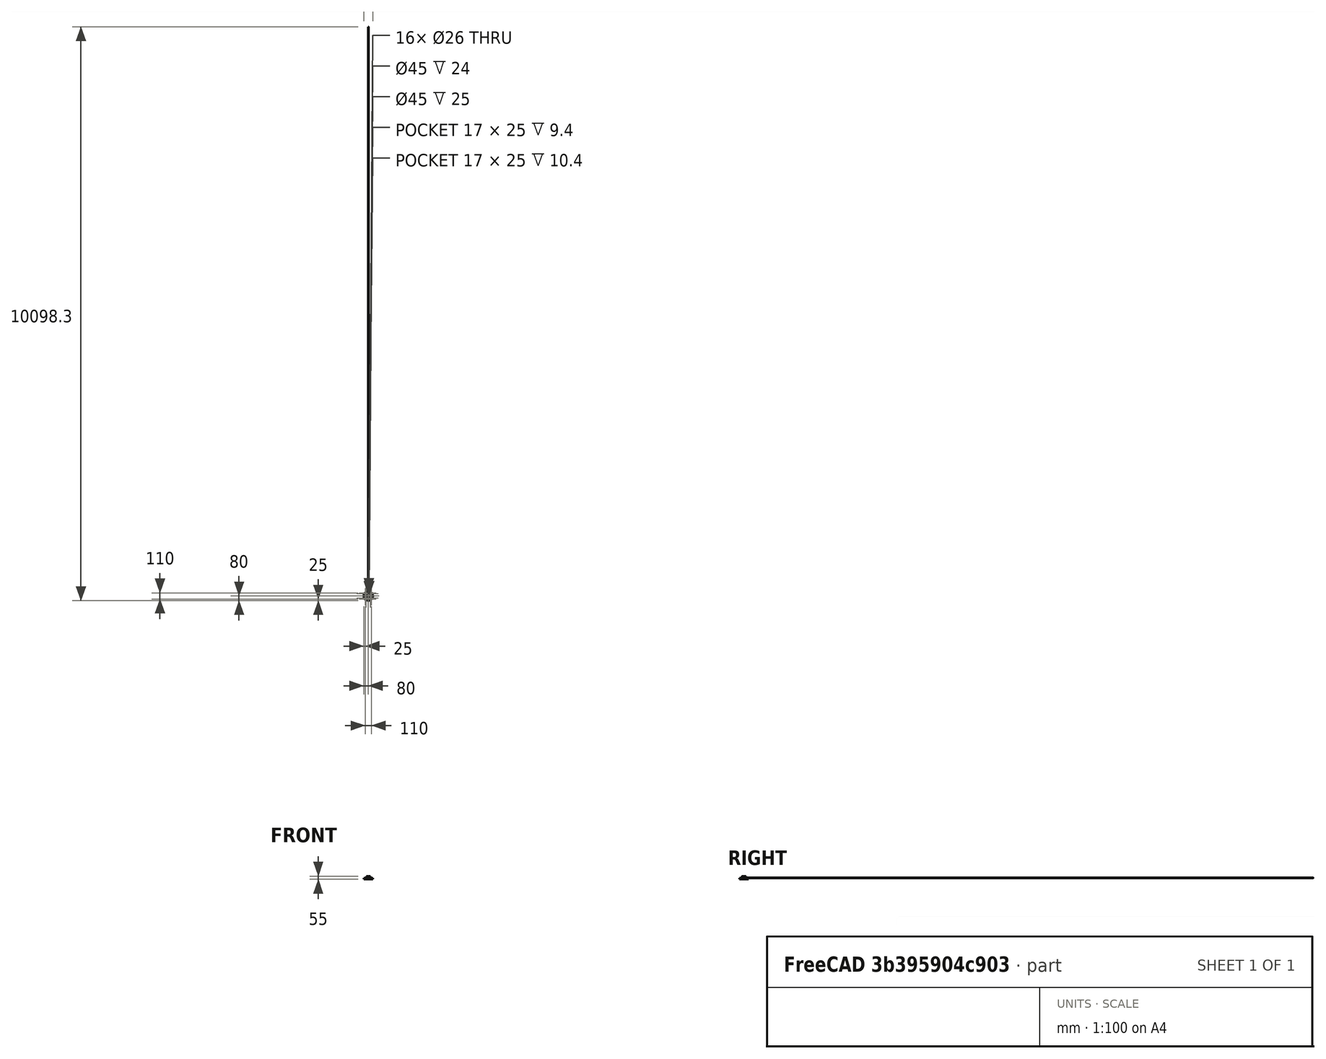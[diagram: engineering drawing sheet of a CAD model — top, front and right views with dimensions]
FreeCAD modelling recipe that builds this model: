
FCSTD DOCUMENT  (FreeCAD 0.16R)
Label: tubknobtest
License: All rights reserved
LicenseURL: http://en.wikipedia.org/wiki/All_rights_reserved
objects: Sketcher::SketchObject×9, PartDesign::Pocket×6, PartDesign::Pad×2, PartDesign::Chamfer×2, PartDesign::PolarPattern×1, PartDesign::Fillet×1, Mesh::Feature×1
note: 29 computed .brp shape members not serialized (recipe doc carries the construction recipe); baked Part::Feature solids carry a one-line shape summary decoded from their .brp

FEATURE [Sketcher::SketchObject] Sketch
  sketch-geometry (1):
    g0: Circle CenterX=0 CenterY=0 CenterZ=0 NormalX=0 NormalY=0 NormalZ=1 Radius=80
  constraints (2):
    c: Coincident(g0,g-1)
    c: Radius(g0) = 80
FEATURE [PartDesign::Pad] Pad
  Length = 20
  Length2 = 100
  Sketch = -> Sketch
  Type = 0
FEATURE [Sketcher::SketchObject] Sketch001
  Placement = pos=(0,0,20) rot=(0,0,1;0rad)
  Support = -> Pad [Face3]
  sketch-geometry (1):
    g0: Circle CenterX=0 CenterY=0 CenterZ=0 NormalX=0 NormalY=0 NormalZ=1 Radius=34
  constraints (2):
    c: Coincident(g0,g-1)
    c: Radius(g0) = 34
FEATURE [PartDesign::Pad] Pad001
  Length = 35
  Length2 = 100
  Sketch = -> Sketch001
  Type = 0
FEATURE [Sketcher::SketchObject] Sketch002
  Placement = pos=(0,0,55) rot=(0,0,1;0rad)
  Support = -> Pad001 [Face5]
  sketch-geometry (1):
    g0: Circle CenterX=0 CenterY=0 CenterZ=0 NormalX=0 NormalY=0 NormalZ=1 Radius=22.5
  constraints (2):
    c: Coincident(g0,g-1)
    c: Radius(g0) = 22.5
FEATURE [PartDesign::Pocket] Pocket
  Length = 25
  Sketch = -> Sketch002
  Type = 0
FEATURE [Sketcher::SketchObject] Sketch003
  ExternalGeometry = -> [Pocket]
  Placement = pos=(0,0,30) rot=(0,0,1;0rad)
  Support = -> Pocket [Face7]
  sketch-geometry (5):
    g0: LineSegment StartX=-8.5 StartY=18.3 StartZ=0 EndX=8.5 EndY=18.3 EndZ=0
    g1: LineSegment StartX=8.5 StartY=18.3 StartZ=0 EndX=8.5 EndY=-6.7 EndZ=0
    g2: LineSegment StartX=8.5 StartY=-6.7 StartZ=0 EndX=-8.5 EndY=-6.7 EndZ=0
    g3: LineSegment StartX=-8.5 StartY=-6.7 StartZ=0 EndX=-8.5 EndY=18.3 EndZ=0
    g4: LineSegment [constr] StartX=-146.442 StartY=22.5 StartZ=0 EndX=146.442 EndY=22.5 EndZ=0
  constraints (16):
    c: Coincident(g0,g1)
    c: Coincident(g1,g2)
    c: Coincident(g2,g3)
    c: Coincident(g3,g0)
    c: Horizontal(g0)
    c: Horizontal(g2)
    c: Vertical(g1)
    c: Vertical(g3)
    c: Distance(g0) = 17
    c: Horizontal(g4)
    c: Tangent(g-4,g4)
    c: Distance(g0,g4) = 4.2
    c: Distance(g1) = 25
    c: Symmetric(g1,g2,g-2)
    c: Symmetric(g4,g4,g-2)
    c: Distance(g4) = 292.885
FEATURE [PartDesign::Pocket] Pocket001
  Length = 10.4
  Sketch = -> Sketch003
  Type = 0
FEATURE [Sketcher::SketchObject] Sketch005
  Placement = pos=(0,0,0) rot=(1,0,0;3.14159rad)
  Support = -> Pocket001 [Face2]
  sketch-geometry (1):
    g0: Circle CenterX=55 CenterY=0 CenterZ=0 NormalX=0 NormalY=0 NormalZ=1 Radius=13
  constraints (3):
    c: PointOnObject(g0,g-1)
    c: Radius(g0) = 13
    c: DistanceX(g0) = 55
FEATURE [PartDesign::Pocket] Pocket002
  Length = 5
  Sketch = -> Sketch005
  Type = 1
FEATURE [PartDesign::PolarPattern] PolarPattern
  Angle = 360
  Axis = -> Sketch005 [N_Axis]
  Occurrences = 8
  Originals = -> [Pocket002]
FEATURE [Sketcher::SketchObject] Sketch006
  Placement = pos=(-8.5,0,0) rot=(0.57735,0.57735,0.57735;2.0944rad)
  Support = -> PolarPattern [Face19]
  sketch-geometry (1):
    g0: Circle CenterX=0 CenterY=24.5 CenterZ=0 NormalX=0 NormalY=0 NormalZ=1 Radius=2
  constraints (3):
    c: Radius(g0) = 2
    c: PointOnObject(g0,g-2)
    c: DistanceY(g0) = 24.5
FEATURE [PartDesign::Pocket] Pocket003
  Length = 20
  Sketch = -> Sketch006
  Type = 0
FEATURE [Sketcher::SketchObject] Sketch007
  Placement = pos=(0,0,0) rot=(1,0,0;3.14159rad)
  Support = -> Pocket003 [Face2]
  sketch-geometry (7):
    g0: LineSegment StartX=-19.085 StartY=6.10318 StartZ=0 EndX=0 EndY=35.1301 EndZ=0
    g1: LineSegment StartX=0 StartY=35.1301 StartZ=0 EndX=19.085 EndY=6.10318 EndZ=0
    g2: LineSegment StartX=19.085 StartY=6.10318 StartZ=0 EndX=8.88636 EndY=6.10318 EndZ=0
    g3: LineSegment StartX=8.88636 StartY=6.10318 StartZ=0 EndX=8.88636 EndY=-23.5121 EndZ=0
    g4: LineSegment StartX=8.88636 StartY=-23.5121 StartZ=0 EndX=-8.88636 EndY=-23.5121 EndZ=0
    g5: LineSegment StartX=-8.88636 StartY=-23.5121 StartZ=0 EndX=-8.88636 EndY=6.10318 EndZ=0
    g6: LineSegment StartX=-8.88636 StartY=6.10318 StartZ=0 EndX=-19.085 EndY=6.10318 EndZ=0
  constraints (14):
    c: Coincident(g0,g1)
    c: Coincident(g1,g2)
    c: Coincident(g2,g3)
    c: Coincident(g3,g4)
    c: Coincident(g4,g5)
    c: Vertical(g5)
    c: Coincident(g5,g6)
    c: Coincident(g6,g0)
    c: Vertical(g3)
    c: Symmetric(g3,g4,g-2)
    c: Horizontal(g2)
    c: Horizontal(g6)
    c: Symmetric(g1,g0,g-2)
    c: PointOnObject(g0,g-2)
FEATURE [PartDesign::Pocket] Pocket004
  Length = 3
  Sketch = -> Sketch007
  Type = 0
FEATURE [PartDesign::Chamfer] Chamfer
  Base = -> Pocket004 [Edge2,Edge4,Edge5,Edge6,Edge7,Edge8,Edge9,Edge10,Edge11,Edge12,Edge13,Edge14,Edge15,Edge16,Edge17,Edge18]
  Size = 2.4
FEATURE [PartDesign::Fillet] Fillet
  Base = -> Chamfer [Edge3,Edge6,Edge7,Edge8,Edge9,Edge10,Edge11,Edge12,Edge13,Edge14]
  Radius = 3
FEATURE [PartDesign::Chamfer] Chamfer001
  Base = -> Fillet [Edge104,Edge110,Edge109,Edge108,Edge107]
  Size = 1
FEATURE [Sketcher::SketchObject] Sketch008
  Placement = pos=(0,18.3,0) rot=(1,0,0;1.5708rad)
  Support = -> Chamfer001 [Face23]
  sketch-geometry (1):
    g0: Circle CenterX=0 CenterY=25 CenterZ=0 NormalX=0 NormalY=0 NormalZ=1 Radius=2
  constraints (3):
    c: Radius(g0) = 2
    c: DistanceY(g0) = 25
    c: PointOnObject(g0,g-2)
FEATURE [PartDesign::Pocket] Pocket005
  Length = 5
  Sketch = -> Sketch008
  Type = 1
FEATURE [Mesh::Feature] Mesh  label="Pocket005 (Meshed)"
FEATURE [Sketcher::SketchObject] Sketch009
